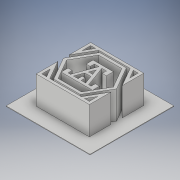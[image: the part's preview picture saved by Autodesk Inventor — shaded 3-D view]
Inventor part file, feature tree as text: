
AUTODESK INVENTOR PART (.ipt)
format: ipt  version: 2019 (Build 230136000, 136)  size: 229,888 bytes
history: native  units: mm
features: extrude x2, sketch x2
ambient origin geometry x8: Origin, YZ Plane, XZ Plane, XY Plane, X Axis, Y Axis, Z Axis, Center Point
bodies: Solid1 (feature_tree)
feature tree (4):
  extrude  "Extrusion1"  Depth=20.0mm
  extrude  "Extrusion2"  Depth=1.0mm
  sketch  "Sketch1"  dims[d0=20.0mm d1=20.0mm]
  sketch  "Sketch2"  dims[d2=0.5mm d3=1.0mm d4=1.5mm d5=1.0mm d6=1.5mm d7=1.0mm d9=12.217305mm d13=1.5mm d14=1.5mm d15=1.0mm d16=1.0mm d17=2.0mm d18=1.0mm d19=2.5mm d23=1.0mm d26=2.5mm d27=10.0mm d28=0.0mm d29=0.5mm d30=1.0mm d32=1.0mm d33=1.0mm d34=1.0mm d35=30.0mm d36=30.0mm d37=0.2mm d38=0.0mm]
